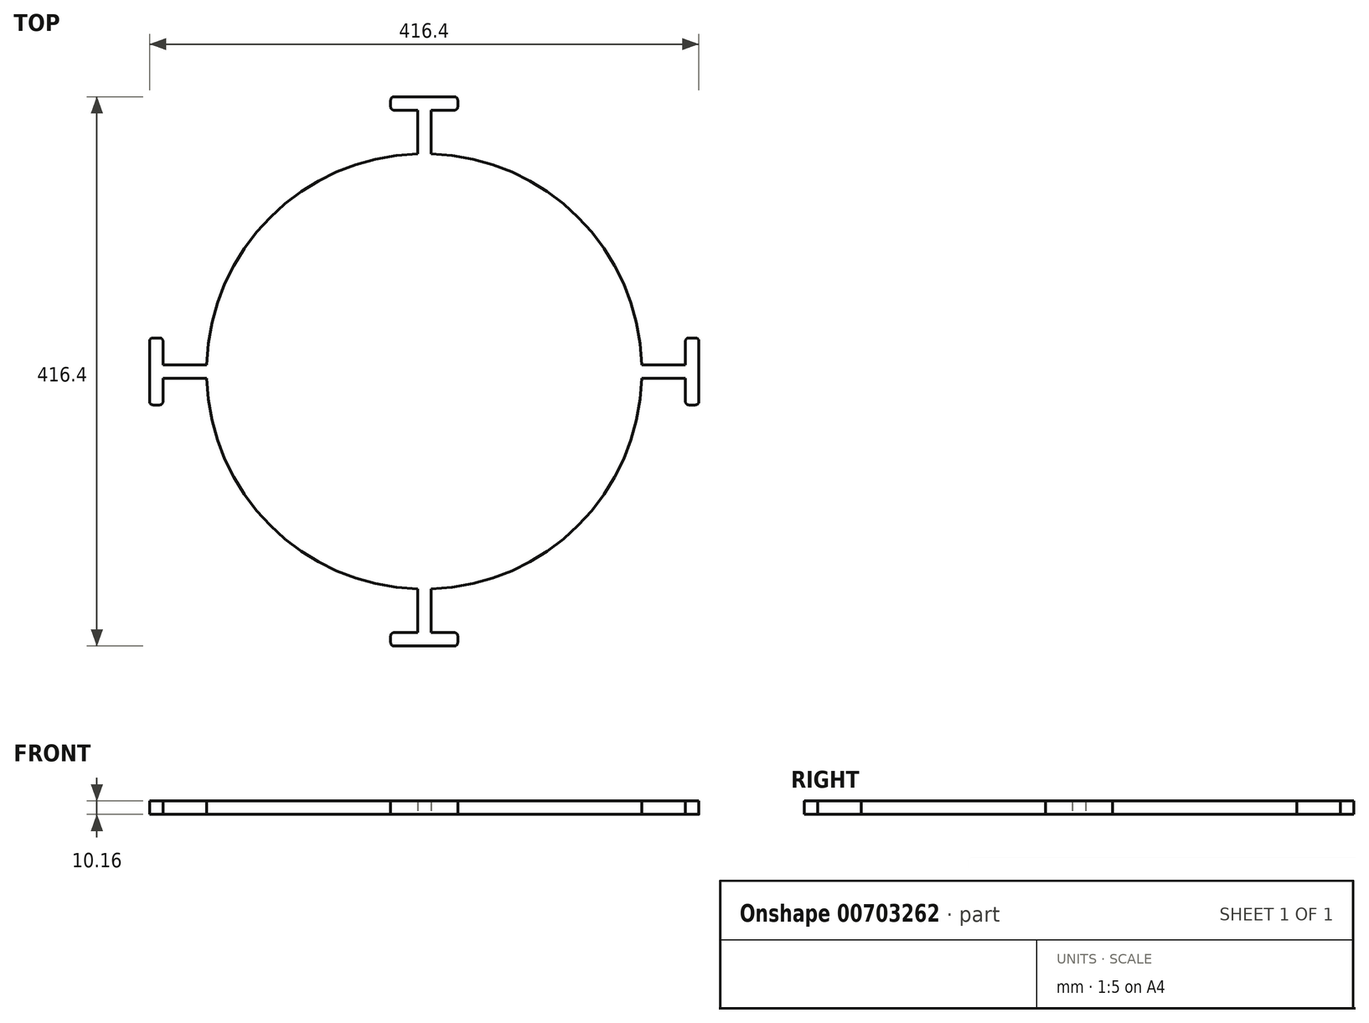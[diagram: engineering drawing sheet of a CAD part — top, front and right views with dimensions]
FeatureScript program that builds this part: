
annotation { "Feature Type Name" : "Feature", "Feature Type Description" : "" }
export const myFeature = defineFeature(function(context is Context, id is Id, definition is map)
    precondition{}
    {
        {
            var Q0;
            Q0=qCreatedBy(makeId("Top.planeOp"),FACE);
            var sketch = newSketch(context, id + "F0", { "sketchPlane" : qUnion([Q0])});
            skCircle(sketch, "E0", {"center": v(0, 0) * mm, "radius": 165.1 * mm});
            skLineSegment(sketch, "E1", {"start": v(121.32, 0) * mm, "end": v(165.1, 0) * mm});
            skLineSegment(sketch, "E2", {"start": v(165.02, 5.08) * mm, "end": v(203.12, 5.08) * mm});
            skLineSegment(sketch, "E3.MirrorCS", {"start": v(165.02, -5.08) * mm, "end": v(203.12, -5.08) * mm});
            skArc(sketch, "E4", {"start": v(203.12, -5.08) * mm, "mid": v(208.2, 0) * mm, "end": v(203.12, 5.08) * mm});
            skLineSegment(sketch, "E5", {"start": v(0, 0) * mm, "end": v(0, 178.9) * mm});
            skLineSegment(sketch, "E6", {"start": v(0, 0) * mm, "end": v(64.11, 0) * mm});
            skLineSegment(sketch, "E7.MirrorCS", {"start": v(-165.02, 5.08) * mm, "end": v(-203.12, 5.08) * mm});
            skLineSegment(sketch, "E8.MirrorCS", {"start": v(-165.02, -5.08) * mm, "end": v(-203.12, -5.08) * mm});
            skArc(sketch, "E9.MirrorCS", {"start": v(-203.12, -5.08) * mm, "mid": v(-208.2, 0) * mm, "end": v(-203.12, 5.08) * mm});
            skLineSegment(sketch, "E10", {"start": v(-5.08, 165.02) * mm, "end": v(-5.08, 203.12) * mm});
            skLineSegment(sketch, "E11.MirrorCS", {"start": v(5.08, 165.02) * mm, "end": v(5.08, 203.12) * mm});
            skArc(sketch, "E12", {"start": v(5.08, 203.12) * mm, "mid": v(0, 208.2) * mm, "end": v(-5.08, 203.12) * mm});
            skLineSegment(sketch, "E13.MirrorCS", {"start": v(5.08, -165.02) * mm, "end": v(5.08, -203.12) * mm});
            skArc(sketch, "E14.MirrorCS", {"start": v(5.08, -203.12) * mm, "mid": v(0, -208.2) * mm, "end": v(-5.08, -203.12) * mm});
            skLineSegment(sketch, "E15.MirrorCS", {"start": v(-5.08, -165.02) * mm, "end": v(-5.08, -203.12) * mm});
            skLineSegment(sketch, "E16.bottom", {"start": v(-22.86, 208.2) * mm, "end": v(22.86, 208.2) * mm});
            skLineSegment(sketch, "E16.top", {"start": v(-22.86, 198.04) * mm, "end": v(22.86, 198.04) * mm});
            skLineSegment(sketch, "E16.left", {"start": v(-25.4, 205.66) * mm, "end": v(-25.4, 200.58) * mm});
            skLineSegment(sketch, "E16.right", {"start": v(25.4, 205.66) * mm, "end": v(25.4, 200.58) * mm});
            skLineSegment(sketch, "E17.MirrorCS", {"start": v(-22.86, -198.04) * mm, "end": v(22.86, -198.04) * mm});
            skLineSegment(sketch, "E18.MirrorCS", {"start": v(-22.86, -208.2) * mm, "end": v(22.86, -208.2) * mm});
            skLineSegment(sketch, "E19.MirrorCS", {"start": v(25.4, -205.66) * mm, "end": v(25.4, -200.58) * mm});
            skLineSegment(sketch, "E20.MirrorCS", {"start": v(-25.4, -205.66) * mm, "end": v(-25.4, -200.58) * mm});
            skLineSegment(sketch, "E21.bottom", {"start": v(205.66, 25.4) * mm, "end": v(200.58, 25.4) * mm});
            skLineSegment(sketch, "E21.top", {"start": v(205.66, -25.4) * mm, "end": v(200.58, -25.4) * mm});
            skLineSegment(sketch, "E21.left", {"start": v(208.2, 22.86) * mm, "end": v(208.2, -22.86) * mm});
            skLineSegment(sketch, "E21.right", {"start": v(198.04, 22.86) * mm, "end": v(198.04, -22.86) * mm});
            skPoint(sketch, "E21.cornerSnap0", {"position": v(208.2, 0) * mm});
            skLineSegment(sketch, "E22.MirrorCS", {"start": v(-208.2, 22.86) * mm, "end": v(-208.2, -22.86) * mm});
            skLineSegment(sketch, "E23.MirrorCS", {"start": v(-205.66, 25.4) * mm, "end": v(-200.58, 25.4) * mm});
            skLineSegment(sketch, "E24.MirrorCS", {"start": v(-205.66, -25.4) * mm, "end": v(-200.58, -25.4) * mm});
            skLineSegment(sketch, "E25.MirrorCS", {"start": v(-198.04, 22.86) * mm, "end": v(-198.04, -22.86) * mm});
            skPoint(sketch, "E26.visualSharp", {"position": v(25.4, 208.2) * mm});
            skArc(sketch, "E26.filletArc", {"start": v(25.4, 205.66) * mm, "mid": v(24.66, 207.46) * mm, "end": v(22.86, 208.2) * mm});
            skPoint(sketch, "E27.visualSharp", {"position": v(25.4, 198.04) * mm});
            skArc(sketch, "E27.filletArc", {"start": v(22.86, 198.04) * mm, "mid": v(24.66, 198.79) * mm, "end": v(25.4, 200.58) * mm});
            skPoint(sketch, "E28.visualSharp", {"position": v(-25.4, 208.2) * mm});
            skArc(sketch, "E28.filletArc", {"start": v(-22.86, 208.2) * mm, "mid": v(-24.66, 207.46) * mm, "end": v(-25.4, 205.66) * mm});
            skPoint(sketch, "E29.visualSharp", {"position": v(-25.4, 198.04) * mm});
            skArc(sketch, "E29.filletArc", {"start": v(-25.4, 200.58) * mm, "mid": v(-24.66, 198.79) * mm, "end": v(-22.86, 198.04) * mm});
            skPoint(sketch, "E30.visualSharp", {"position": v(208.2, 25.4) * mm});
            skArc(sketch, "E30.filletArc", {"start": v(208.2, 22.86) * mm, "mid": v(207.46, 24.66) * mm, "end": v(205.66, 25.4) * mm});
            skPoint(sketch, "E31.visualSharp", {"position": v(198.04, 25.4) * mm});
            skArc(sketch, "E31.filletArc", {"start": v(200.58, 25.4) * mm, "mid": v(198.79, 24.66) * mm, "end": v(198.04, 22.86) * mm});
            skPoint(sketch, "E32.visualSharp", {"position": v(208.2, -25.4) * mm});
            skArc(sketch, "E32.filletArc", {"start": v(205.66, -25.4) * mm, "mid": v(207.46, -24.66) * mm, "end": v(208.2, -22.86) * mm});
            skPoint(sketch, "E33.visualSharp", {"position": v(25.4, -198.04) * mm});
            skArc(sketch, "E33.filletArc", {"start": v(25.4, -200.58) * mm, "mid": v(24.66, -198.79) * mm, "end": v(22.86, -198.04) * mm});
            skPoint(sketch, "E34.visualSharp", {"position": v(25.4, -208.2) * mm});
            skArc(sketch, "E34.filletArc", {"start": v(22.86, -208.2) * mm, "mid": v(24.66, -207.46) * mm, "end": v(25.4, -205.66) * mm});
            skPoint(sketch, "E35.visualSharp", {"position": v(-25.4, -208.2) * mm});
            skArc(sketch, "E35.filletArc", {"start": v(-25.4, -205.66) * mm, "mid": v(-24.66, -207.46) * mm, "end": v(-22.86, -208.2) * mm});
            skPoint(sketch, "E36.visualSharp", {"position": v(-25.4, -198.04) * mm});
            skArc(sketch, "E36.filletArc", {"start": v(-22.86, -198.04) * mm, "mid": v(-24.66, -198.79) * mm, "end": v(-25.4, -200.58) * mm});
            skPoint(sketch, "E37.visualSharp", {"position": v(-198.04, -25.4) * mm});
            skArc(sketch, "E37.filletArc", {"start": v(-200.58, -25.4) * mm, "mid": v(-198.79, -24.66) * mm, "end": v(-198.04, -22.86) * mm});
            skPoint(sketch, "E38.visualSharp", {"position": v(-208.2, -25.4) * mm});
            skArc(sketch, "E38.filletArc", {"start": v(-208.2, -22.86) * mm, "mid": v(-207.46, -24.66) * mm, "end": v(-205.66, -25.4) * mm});
            skPoint(sketch, "E39.visualSharp", {"position": v(-198.04, 25.4) * mm});
            skArc(sketch, "E39.filletArc", {"start": v(-198.04, 22.86) * mm, "mid": v(-198.79, 24.66) * mm, "end": v(-200.58, 25.4) * mm});
            skPoint(sketch, "E40.visualSharp", {"position": v(-208.2, 25.4) * mm});
            skArc(sketch, "E40.filletArc", {"start": v(-205.66, 25.4) * mm, "mid": v(-207.46, 24.66) * mm, "end": v(-208.2, 22.86) * mm});
            skPoint(sketch, "E41.visualSharp", {"position": v(198.04, -25.4) * mm});
            skArc(sketch, "E41.filletArc", {"start": v(198.04, -22.86) * mm, "mid": v(198.79, -24.66) * mm, "end": v(200.58, -25.4) * mm});
            skSolve(sketch);
        }
        {
            var Q0;
            {var subQ0=sQuery(id+"F0.wireOp",EDGE,"E0");var subQ5=makeQuery(id+"F0.imprint","IMPRINT",VERTEX,{"disambiguationData":[OD(0.0)],"derivedFrom":subQ0});Q0=makeQuery(id+"F0.imprint","IMPRINT",FACE,{"disambiguationData":[TD([[makeQuery(id+"F0.imprint","IMPRINT",EDGE,{"disambiguationData":[TD([[subQ5,-1.0]])],"derivedFrom":subQ0}),1.0]])]});}
            var Q1;
            {var subQ0=sQuery(id+"F0.wireOp",EDGE,"E0");var subQ1=makeQuery(id+"F0.imprint","IMPRINT",VERTEX,{"disambiguationData":[OD(0.0)],"derivedFrom":subQ0});Q1=makeQuery(id+"F0.imprint","IMPRINT",FACE,{"disambiguationData":[TD([[makeQuery(id+"F0.imprint","IMPRINT",EDGE,{"disambiguationData":[TD([[subQ1,-1.0]])],"derivedFrom":subQ0}),-1.0]])]});}
            var Q2;
            {var subQ0=sQuery(id+"F0.wireOp",EDGE,"E7.MirrorCS");var subQ1=sQuery(id+"F0.wireOp",EDGE,"E0");var subQ2=makeQuery(id+"F0.imprint","INTERSECT",VERTEX,{"derivedFrom":[subQ1,subQ0]});Q2=makeQuery(id+"F0.imprint","IMPRINT",FACE,{"disambiguationData":[TD([[makeQuery(id+"F0.imprint","IMPRINT",EDGE,{"disambiguationData":[TD([[subQ2,-1.0]])],"derivedFrom":subQ1}),-1.0]])]});}
            var Q3;
            Q3=makeQuery(id+"F0.imprint","IMPRINT",FACE,{"disambiguationData":[TD([[makeQuery(id+"F0.imprint","IMPRINT",EDGE,{"derivedFrom":sQuery(id+"F0.wireOp",EDGE,"E23.MirrorCS")}),-1.0]])]});
            var Q4;
            Q4=makeQuery(id+"F0.imprint","IMPRINT",FACE,{"disambiguationData":[TD([[makeQuery(id+"F0.imprint","IMPRINT",EDGE,{"derivedFrom":sQuery(id+"F0.wireOp",EDGE,"E24.MirrorCS")}),1.0]])]});
            var Q5;
            {var subQ0=sQuery(id+"F0.wireOp",EDGE,"E9.MirrorCS");var subQ1=sQuery(id+"F0.wireOp",EDGE,"E7.MirrorCS");var subQ2=makeQuery(id+"F0.imprint","INTERSECT",VERTEX,{"derivedFrom":[subQ1,subQ0]});Q5=makeQuery(id+"F0.imprint","IMPRINT",FACE,{"disambiguationData":[TD([[makeQuery(id+"F0.imprint","IMPRINT",EDGE,{"disambiguationData":[TD([[subQ2,1.0]])],"derivedFrom":subQ1}),1.0]])]});}
            var Q6;
            {var subQ0=sQuery(id+"F0.wireOp",EDGE,"E13.MirrorCS");var subQ1=sQuery(id+"F0.wireOp",EDGE,"E0");var subQ2=makeQuery(id+"F0.imprint","INTERSECT",VERTEX,{"derivedFrom":[subQ1,subQ0]});Q6=makeQuery(id+"F0.imprint","IMPRINT",FACE,{"disambiguationData":[TD([[makeQuery(id+"F0.imprint","IMPRINT",EDGE,{"disambiguationData":[TD([[subQ2,1.0]])],"derivedFrom":subQ1}),-1.0]])]});}
            var Q7;
            Q7=makeQuery(id+"F0.imprint","IMPRINT",FACE,{"disambiguationData":[TD([[makeQuery(id+"F0.imprint","IMPRINT",EDGE,{"derivedFrom":sQuery(id+"F0.wireOp",EDGE,"E19.MirrorCS")}),1.0]])]});
            var Q8;
            Q8=makeQuery(id+"F0.imprint","IMPRINT",FACE,{"disambiguationData":[TD([[makeQuery(id+"F0.imprint","IMPRINT",EDGE,{"derivedFrom":sQuery(id+"F0.wireOp",EDGE,"E20.MirrorCS")}),-1.0]])]});
            var Q9;
            {var subQ1=sQuery(id+"F0.wireOp",EDGE,"E14.MirrorCS");var subQ6=sQuery(id+"F0.wireOp",EDGE,"E13.MirrorCS");var subQ8=makeQuery(id+"F0.imprint","INTERSECT",VERTEX,{"derivedFrom":[subQ6,subQ1]});Q9=makeQuery(id+"F0.imprint","IMPRINT",FACE,{"disambiguationData":[TD([[makeQuery(id+"F0.imprint","IMPRINT",EDGE,{"disambiguationData":[TD([[subQ8,1.0]])],"derivedFrom":subQ6}),-1.0]])]});}
            var Q10;
            Q10=makeQuery(id+"F0.imprint","IMPRINT",FACE,{"disambiguationData":[TD([[makeQuery(id+"F0.imprint","IMPRINT",EDGE,{"derivedFrom":sQuery(id+"F0.wireOp",EDGE,"E21.bottom")}),1.0]])]});
            var Q11;
            {var subQ0=sQuery(id+"F0.wireOp",EDGE,"E4");var subQ1=sQuery(id+"F0.wireOp",EDGE,"E2");var subQ2=makeQuery(id+"F0.imprint","INTERSECT",VERTEX,{"derivedFrom":[subQ1,subQ0]});Q11=makeQuery(id+"F0.imprint","IMPRINT",FACE,{"disambiguationData":[TD([[makeQuery(id+"F0.imprint","IMPRINT",EDGE,{"disambiguationData":[TD([[subQ2,1.0]])],"derivedFrom":subQ1}),-1.0]])]});}
            var Q12;
            {var subQ0=sQuery(id+"F0.wireOp",EDGE,"E21.top");Q12=makeQuery(id+"F0.imprint","IMPRINT",FACE,{"disambiguationData":[TD([[makeQuery(id+"F0.imprint","IMPRINT",EDGE,{"derivedFrom":subQ0}),-1.0]])]});}
            var Q13;
            Q13=makeQuery(id+"F0.imprint","IMPRINT",FACE,{"disambiguationData":[TD([[makeQuery(id+"F0.imprint","IMPRINT",EDGE,{"derivedFrom":sQuery(id+"F0.wireOp",EDGE,"E16.right")}),-1.0]])]});
            var Q14;
            {var subQ1=sQuery(id+"F0.wireOp",EDGE,"E0");var subQ5=makeQuery(id+"F0.imprint","IMPRINT",VERTEX,{"disambiguationData":[OD(1.0)],"derivedFrom":subQ1});Q14=makeQuery(id+"F0.imprint","IMPRINT",FACE,{"disambiguationData":[TD([[makeQuery(id+"F0.imprint","IMPRINT",EDGE,{"disambiguationData":[TD([[subQ5,1.0]])],"derivedFrom":subQ1}),-1.0]])]});}
            var Q15;
            Q15=makeQuery(id+"F0.imprint","IMPRINT",FACE,{"disambiguationData":[TD([[makeQuery(id+"F0.imprint","IMPRINT",EDGE,{"derivedFrom":sQuery(id+"F0.wireOp",EDGE,"E16.left")}),1.0]])]});
            var Q16;
            {var subQ0=sQuery(id+"F0.wireOp",EDGE,"E12");var subQ1=sQuery(id+"F0.wireOp",EDGE,"E10");var subQ2=makeQuery(id+"F0.imprint","INTERSECT",VERTEX,{"derivedFrom":[subQ1,subQ0]});Q16=makeQuery(id+"F0.imprint","IMPRINT",FACE,{"disambiguationData":[TD([[makeQuery(id+"F0.imprint","IMPRINT",EDGE,{"disambiguationData":[TD([[subQ2,1.0]])],"derivedFrom":subQ1}),-1.0]])]});}
            extrude(context, id + "F1", {"entities" : qUnion([Q0, Q1, Q2, Q3, Q4, Q5, Q6, Q7, Q8, Q9, Q10, Q11, Q12, Q13, Q14, Q15, Q16]), "depth" : 10.16 * mm, "offsetDistance" : 25.4 * mm});
        }
    });
